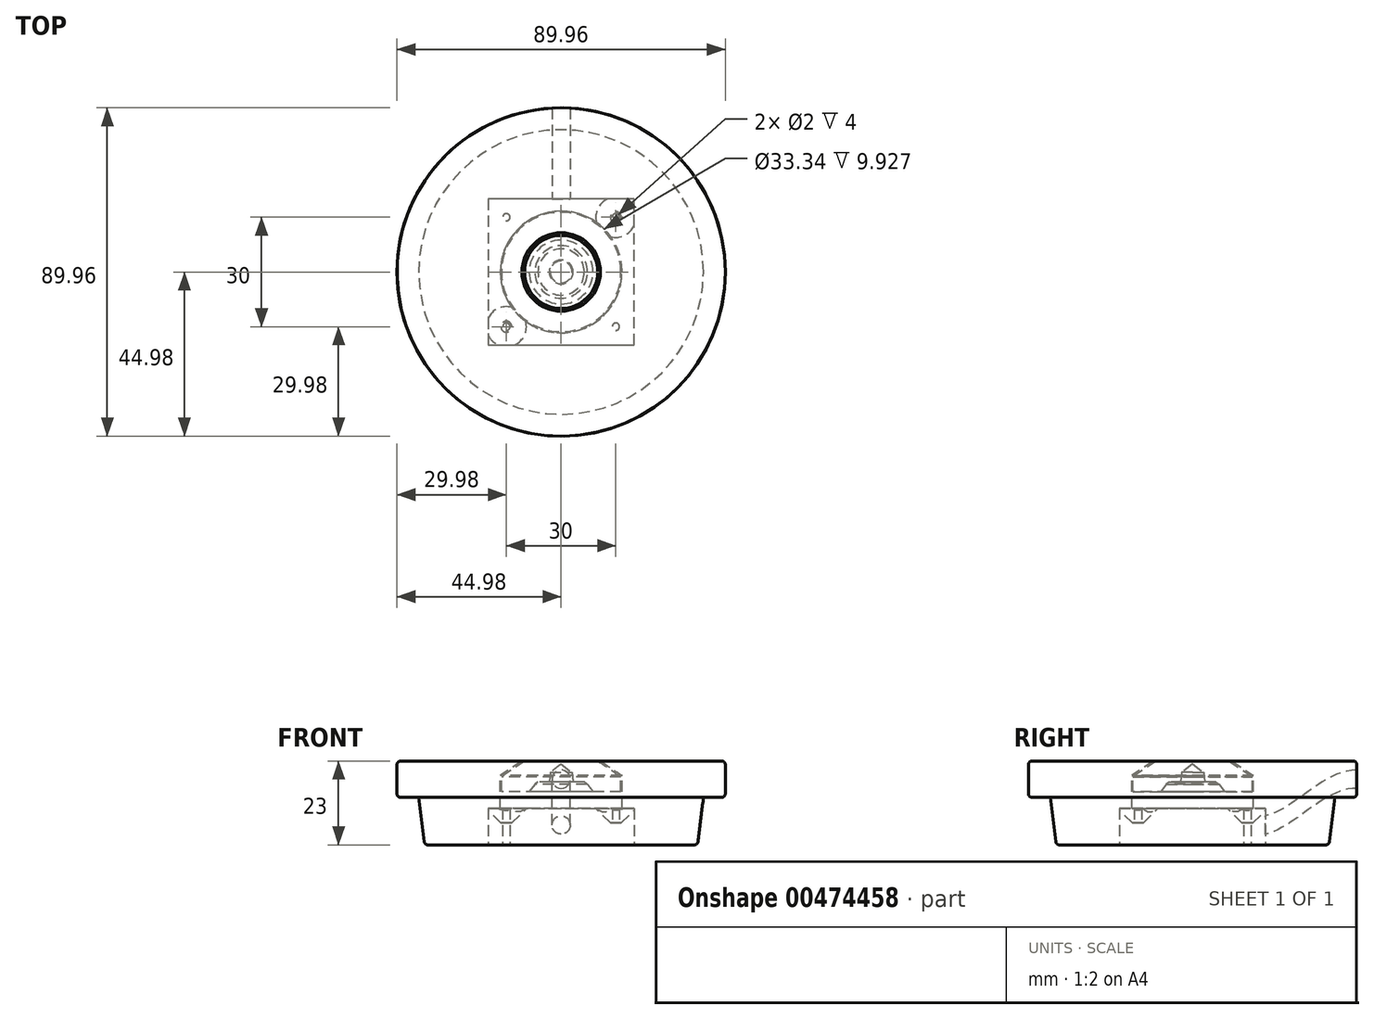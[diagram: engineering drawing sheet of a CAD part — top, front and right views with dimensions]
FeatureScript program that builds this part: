
annotation { "Feature Type Name" : "Feature", "Feature Type Description" : "" }
export const myFeature = defineFeature(function(context is Context, id is Id, definition is map)
    precondition{}
    {
        {
            var Q0;
            Q0=qCreatedBy(makeId("Right.planeOp"),FACE);
            var sketch = newSketch(context, id + "F0", { "sketchPlane" : qUnion([Q0])});
            skLineSegment(sketch, "E0", {"start": v(0, 0) * mm, "end": v(10, 0) * mm});
            skLineSegment(sketch, "E1", {"start": v(16.67, -4.03) * mm, "end": v(16.67, -10) * mm});
            skLineSegment(sketch, "E2", {"start": v(16.67, -10) * mm, "end": v(10, -10) * mm});
            skLineSegment(sketch, "E3", {"start": v(5, -3.55) * mm, "end": v(0, -3.55) * mm, "construction": true});
            skLineSegment(sketch, "E4", {"start": v(0, -3.55) * mm, "end": v(0, 0) * mm});
            skLineSegment(sketch, "E5.0", {"start": v(16.37, -4.33) * mm, "end": v(16.37, -10) * mm, "construction": true});
            skLineSegment(sketch, "E6", {"start": v(10.74, 0) * mm, "end": v(43.98, 0) * mm});
            skLineSegment(sketch, "E7", {"start": v(44.98, -1) * mm, "end": v(44.98, -9) * mm});
            skLineSegment(sketch, "E8", {"start": v(43.98, -10) * mm, "end": v(39, -10) * mm});
            skPoint(sketch, "E9.visualSharp", {"position": v(10, -3.55) * mm});
            skLineSegment(sketch, "E10", {"start": v(10, 0) * mm, "end": v(16.37, -4.33) * mm});
            skLineSegment(sketch, "E11.0", {"start": v(10.74, 0) * mm, "end": v(16.67, -4.03) * mm});
            skLineSegment(sketch, "E12", {"start": v(7.2, -6.38) * mm, "end": v(10, -10) * mm});
            skLineSegment(sketch, "E13", {"start": v(39, -10) * mm, "end": v(37.5, -22.12) * mm});
            skLineSegment(sketch, "E14", {"start": v(36.5, -23) * mm, "end": v(17.67, -23) * mm});
            skLineSegment(sketch, "E15", {"start": v(16.67, -22) * mm, "end": v(16.67, -10) * mm});
            skPoint(sketch, "E16.visualSharp", {"position": v(44.98, 0) * mm});
            skArc(sketch, "E16.filletArc", {"start": v(44.98, -1) * mm, "mid": v(44.69, -0.3) * mm, "end": v(43.98, 0) * mm});
            skPoint(sketch, "E17.visualSharp", {"position": v(44.98, -10) * mm});
            skArc(sketch, "E17.filletArc", {"start": v(43.98, -10) * mm, "mid": v(44.69, -9.7) * mm, "end": v(44.98, -9) * mm});
            skPoint(sketch, "E18.visualSharp", {"position": v(40.48, -10) * mm});
            skPoint(sketch, "E19.visualSharp", {"position": v(40.5, -23) * mm});
            skArc(sketch, "E19.filletArc", {"start": v(36.5, -23) * mm, "mid": v(37.17, -22.75) * mm, "end": v(37.5, -22.12) * mm});
            skPoint(sketch, "E20.visualSharp", {"position": v(16.67, -23) * mm});
            skArc(sketch, "E20.filletArc", {"start": v(16.67, -22) * mm, "mid": v(16.96, -22.7) * mm, "end": v(17.67, -23) * mm});
            skLineSegment(sketch, "E21", {"start": v(0, 0) * mm, "end": v(0, -40.81) * mm, "construction": true});
            skLineSegment(sketch, "E22", {"start": v(37.5, -22.12) * mm, "end": v(37.5, -26.5) * mm, "construction": true});
            skFitSpline(sketch, "E23", {"points": [v(44.98, -5) * mm, v(16.67, -18) * mm], "startDerivative": vector(-31.15, 0) * mm, "endDerivative": vector(-31.15, 0) * mm});
            skLineSegment(sketch, "E24", {"start": v(16.67, -10) * mm, "end": v(0, -10) * mm, "construction": true});
            skLineSegment(sketch, "E25", {"start": v(0, -10) * mm, "end": v(6, -10) * mm});
            skLineSegment(sketch, "E26", {"start": v(6, -10) * mm, "end": v(6, -6.7) * mm, "construction": true});
            skLineSegment(sketch, "E27", {"start": v(6, -6.7) * mm, "end": v(0, -6.7) * mm, "construction": true});
            skLineSegment(sketch, "E28", {"start": v(3, -6.7) * mm, "end": v(3, -3.55) * mm, "construction": true});
            skLineSegment(sketch, "E29", {"start": v(3, -3.55) * mm, "end": v(0, -3.55) * mm, "construction": true});
            skLineSegment(sketch, "E30", {"start": v(3, -6.7) * mm, "end": v(3, -3.15) * mm});
            skLineSegment(sketch, "E31", {"start": v(3, -3.15) * mm, "end": v(0, -3.15) * mm, "construction": true});
            skLineSegment(sketch, "E32", {"start": v(0, -11.2) * mm, "end": v(11, -11.2) * mm, "construction": true});
            skLineSegment(sketch, "E33", {"start": v(16.37, -8.4) * mm, "end": v(8.77, -8.4) * mm});
            skLineSegment(sketch, "E34", {"start": v(7.2, -6.38) * mm, "end": v(6.36, -5.74) * mm});
            skLineSegment(sketch, "E35", {"start": v(3, -3.15) * mm, "end": v(0, -0.84) * mm});
            skLineSegment(sketch, "E36", {"start": v(16.37, -4.33) * mm, "end": v(16.37, -8.4) * mm});
            skLineSegment(sketch, "E37", {"start": v(6.36, -5.74) * mm, "end": v(3.27, -5.74) * mm});
            skLineSegment(sketch, "E38", {"start": v(3.27, -5.74) * mm, "end": v(3, -3.15) * mm});
            skLineSegment(sketch, "E39.trimOffspring", {"start": v(3.52, -3.55) * mm, "end": v(3, -3.15) * mm});
            skSolve(sketch);
        }
        {
            var Q0;
            Q0=makeQuery(id+"F0.imprint","IMPRINT",FACE,{"disambiguationData":[TD([[makeQuery(id+"F0.imprint","IMPRINT",EDGE,{"derivedFrom":sQuery(id+"F0.wireOp",EDGE,"E0")}),-1.0]])]});
            var Q1;
            Q1=makeQuery(id+"F0.imprint","IMPRINT",FACE,{"disambiguationData":[TD([[makeQuery(id+"F0.imprint","IMPRINT",EDGE,{"derivedFrom":sQuery(id+"F0.wireOp",EDGE,"E1")}),1.0]])]});
            var Q2;
            Q2=makeQuery(id+"F0.imprint","IMPRINT",FACE,{"disambiguationData":[TD([[makeQuery(id+"F0.imprint","IMPRINT",EDGE,{"derivedFrom":sQuery(id+"F0.wireOp",EDGE,"E8")}),-1.0]])]});
            var Q3;
            Q3=sQuery(id+"F0.wireOp",EDGE,"E21");
            revolve(context, id + "F1", {"surfaceOperationType" : NewSurfaceOperationType.NEW, "entities" : qUnion([Q0, Q1, Q2]), "axis" : qUnion([Q3]), "revolveType" : RevolveType.FULL});
        }
        {
            var Q0;
            Q0=makeQuery(id+"F1.opRevolve","SWEPT_FACE",FACE,{"disambiguationData":[OSD([sQuery(id+"F0.wireOp",EDGE,"E14")])]});
            var sketch = newSketch(context, id + "F2", { "sketchPlane" : qUnion([Q0])});
            skLineSegment(sketch, "E40.left", {"start": v(0, 0) * mm, "end": v(0, -20) * mm, "construction": true});
            skLineSegment(sketch, "E41.MirrorCS", {"start": v(-20, 0) * mm, "end": v(-20, -20) * mm});
            skLineSegment(sketch, "E42.MirrorCS", {"start": v(0, -20) * mm, "end": v(-20, -20) * mm});
            skLineSegment(sketch, "E43", {"start": v(0, 0) * mm, "end": v(-20, 0) * mm, "construction": true});
            skLineSegment(sketch, "E44.MirrorCS", {"start": v(-20, 0) * mm, "end": v(-20, 20) * mm});
            skLineSegment(sketch, "E45.MirrorCS", {"start": v(0, 20) * mm, "end": v(-20, 20) * mm});
            skLineSegment(sketch, "E46.MirrorCS", {"start": v(20, 0) * mm, "end": v(20, -20) * mm});
            skLineSegment(sketch, "E47.MirrorCS", {"start": v(20, 0) * mm, "end": v(20, 20) * mm});
            skLineSegment(sketch, "E48.MirrorCS", {"start": v(0, 20) * mm, "end": v(20, 20) * mm});
            skLineSegment(sketch, "E49.MirrorCS", {"start": v(0, -20) * mm, "end": v(20, -20) * mm});
            skLineSegment(sketch, "E50", {"start": v(-20, 20) * mm, "end": v(-15, 15) * mm, "construction": true});
            skPoint(sketch, "E51.orphan", {"position": v(-10, 10) * mm});
            skCircle(sketch, "E52", {"center": v(-15, 15) * mm, "radius": 1 * mm});
            skCircle(sketch, "E53", {"center": v(-15, 15) * mm, "radius": 1.5 * mm});
            skCircle(sketch, "E54.MirrorC", {"center": v(-15, -15) * mm, "radius": 1.5 * mm});
            skCircle(sketch, "E55.MirrorC", {"center": v(-15, -15) * mm, "radius": 1 * mm});
            skCircle(sketch, "E56.MirrorC", {"center": v(15, 15) * mm, "radius": 1 * mm});
            skCircle(sketch, "E57.MirrorC", {"center": v(15, 15) * mm, "radius": 1.5 * mm});
            skCircle(sketch, "E58.MirrorC", {"center": v(15, -15) * mm, "radius": 1.5 * mm});
            skCircle(sketch, "E59.MirrorC", {"center": v(15, -15) * mm, "radius": 1 * mm});
            skSolve(sketch);
        }
        {
            var Q0;
            Q0=makeQuery(id+"F2.imprint","IMPRINT",FACE,{"disambiguationData":[TD([[makeQuery(id+"F2.imprint","IMPRINT",EDGE,{"derivedFrom":sQuery(id+"F2.wireOp",EDGE,"E41.MirrorCS")}),1.0]])]});
            var Q1;
            Q1=makeQuery(id+"F2.imprint","IMPRINT",FACE,{"disambiguationData":[TD([[makeQuery(id+"F2.imprint","IMPRINT",EDGE,{"derivedFrom":makeQuery(id+"F1.opRevolve","SWEPT_EDGE",EDGE,{"disambiguationData":[OSD([sQuery(id+"F0.wireOp",EDGE,"E14"),sQuery(id+"F0.wireOp",EDGE,"E20.filletArc")])]})}),-1.0]])]});
            var Q2;
            Q2=makeQuery(id+"F2.imprint","IMPRINT",FACE,{"disambiguationData":[TD([[makeQuery(id+"F2.imprint","IMPRINT",EDGE,{"derivedFrom":sQuery(id+"F2.wireOp",EDGE,"E52")}),1.0]])]});
            var Q3;
            Q3=makeQuery(id+"F2.imprint","IMPRINT",FACE,{"disambiguationData":[TD([[makeQuery(id+"F2.imprint","IMPRINT",EDGE,{"derivedFrom":sQuery(id+"F2.wireOp",EDGE,"E56.MirrorC")}),-1.0]])]});
            var Q4;
            Q4=makeQuery(id+"F2.imprint","IMPRINT",FACE,{"disambiguationData":[TD([[makeQuery(id+"F2.imprint","IMPRINT",EDGE,{"derivedFrom":sQuery(id+"F2.wireOp",EDGE,"E59.MirrorC")}),1.0]])]});
            var Q5;
            Q5=makeQuery(id+"F2.imprint","IMPRINT",FACE,{"disambiguationData":[TD([[makeQuery(id+"F2.imprint","IMPRINT",EDGE,{"derivedFrom":sQuery(id+"F2.wireOp",EDGE,"E55.MirrorC")}),-1.0]])]});
            extrude(context, id + "F3", {"entities" : qUnion([Q0, Q1, Q2, Q3, Q4, Q5]), "operationType" : NewBodyOperationType.REMOVE, "oppositeDirection" : true, "depth" : 10 * mm, "offsetDistance" : 25 * mm});
        }
        {
            var Q0;
            Q0=makeQuery(id+"F2.imprint","IMPRINT",FACE,{"disambiguationData":[TD([[makeQuery(id+"F2.imprint","IMPRINT",EDGE,{"derivedFrom":sQuery(id+"F2.wireOp",EDGE,"E41.MirrorCS")}),1.0]])]});
            var Q1;
            Q1=makeQuery(id+"F2.imprint","IMPRINT",FACE,{"disambiguationData":[TD([[makeQuery(id+"F2.imprint","IMPRINT",EDGE,{"derivedFrom":sQuery(id+"F2.wireOp",EDGE,"E52")}),-1.0]])]});
            var Q2;
            Q2=makeQuery(id+"F2.imprint","IMPRINT",FACE,{"disambiguationData":[TD([[makeQuery(id+"F2.imprint","IMPRINT",EDGE,{"derivedFrom":sQuery(id+"F2.wireOp",EDGE,"E52")}),1.0]])]});
            var Q3;
            Q3=makeQuery(id+"F2.imprint","IMPRINT",FACE,{"disambiguationData":[TD([[makeQuery(id+"F2.imprint","IMPRINT",EDGE,{"derivedFrom":sQuery(id+"F2.wireOp",EDGE,"E56.MirrorC")}),1.0]])]});
            var Q4;
            Q4=makeQuery(id+"F2.imprint","IMPRINT",FACE,{"disambiguationData":[TD([[makeQuery(id+"F2.imprint","IMPRINT",EDGE,{"derivedFrom":sQuery(id+"F2.wireOp",EDGE,"E56.MirrorC")}),-1.0]])]});
            var Q5;
            Q5=makeQuery(id+"F2.imprint","IMPRINT",FACE,{"disambiguationData":[TD([[makeQuery(id+"F2.imprint","IMPRINT",EDGE,{"derivedFrom":sQuery(id+"F2.wireOp",EDGE,"E58.MirrorC")}),1.0]])]});
            var Q6;
            Q6=makeQuery(id+"F2.imprint","IMPRINT",FACE,{"disambiguationData":[TD([[makeQuery(id+"F2.imprint","IMPRINT",EDGE,{"derivedFrom":sQuery(id+"F2.wireOp",EDGE,"E59.MirrorC")}),1.0]])]});
            var Q7;
            Q7=makeQuery(id+"F2.imprint","IMPRINT",FACE,{"disambiguationData":[TD([[makeQuery(id+"F2.imprint","IMPRINT",EDGE,{"derivedFrom":sQuery(id+"F2.wireOp",EDGE,"E54.MirrorC")}),-1.0]])]});
            var Q8;
            Q8=makeQuery(id+"F2.imprint","IMPRINT",FACE,{"disambiguationData":[TD([[makeQuery(id+"F2.imprint","IMPRINT",EDGE,{"derivedFrom":sQuery(id+"F2.wireOp",EDGE,"E55.MirrorC")}),-1.0]])]});
            extrude(context, id + "F4", {"entities" : qUnion([Q0, Q1, Q2, Q3, Q4, Q5, Q6, Q7, Q8]), "operationType" : NewBodyOperationType.REMOVE, "oppositeDirection" : true, "depth" : 6 * mm, "offsetDistance" : 25 * mm});
        }
        {
            var Q0;
            Q0=makeQuery(id+"F3.boolean.opBoolean","COPY",EDGE,{"derivedFrom":makeQuery(id+"F3.opExtrude","CAP_EDGE",EDGE,{"disambiguationData":[OSD([sQuery(id+"F2.wireOp",EDGE,"E54.MirrorC")])],"isStart":false})});
            var Q1;
            Q1=makeQuery(id+"F3.boolean.opBoolean","COPY",EDGE,{"derivedFrom":makeQuery(id+"F3.opExtrude","CAP_EDGE",EDGE,{"disambiguationData":[OSD([sQuery(id+"F2.wireOp",EDGE,"E58.MirrorC")])],"isStart":false})});
            var Q2;
            Q2=makeQuery(id+"F3.boolean.opBoolean","COPY",EDGE,{"derivedFrom":makeQuery(id+"F3.opExtrude","CAP_EDGE",EDGE,{"disambiguationData":[OSD([sQuery(id+"F2.wireOp",EDGE,"E57.MirrorC")])],"isStart":false})});
            var Q3;
            Q3=makeQuery(id+"F3.boolean.opBoolean","COPY",EDGE,{"derivedFrom":makeQuery(id+"F3.opExtrude","CAP_EDGE",EDGE,{"disambiguationData":[OSD([sQuery(id+"F2.wireOp",EDGE,"E53")])],"isStart":false})});
            chamfer(context, id + "F5", {"entities" : qUnion([Q0, Q1, Q2, Q3]), "width" : 4 * mm, "tangentPropagation" : true});
        }
        {
            var Q0;
            Q0=qCreatedBy(makeId("Front.planeOp"),FACE);
            var Q1;
            Q1=sQuery(id+"F0.wireOp",VERTEX,"E23.start");
            cPlane(context, id + "F6", {"entities" : qUnion([Q0, Q1]), "cplaneType" : CPlaneType.PLANE_POINT, "offset" : 25 * mm, "width" : 150 * mm, "height" : 150 * mm});
        }
        {
            var Q0;
            Q0=qCreatedBy(id+"F6.planeOp",FACE);
            var sketch = newSketch(context, id + "F7", { "sketchPlane" : qUnion([Q0])});
            skCircle(sketch, "E60", {"center": v(0, -5) * mm, "radius": 2.5 * mm});
            skSolve(sketch);
        }
        {
            var Q0;
            Q0=makeQuery(id+"F7.imprint","IMPRINT",FACE,{"disambiguationData":[TD([[makeQuery(id+"F7.imprint","IMPRINT",EDGE,{"derivedFrom":sQuery(id+"F7.wireOp",EDGE,"E60")}),1.0]])]});
            var Q1;
            Q1=sQuery(id+"F7.wireOp",EDGE,"E60");
            var Q2;
            Q2=sQuery(id+"F0.wireOp",EDGE,"E23");
            sweep(context, id + "F8", {"operationType" : NewBodyOperationType.REMOVE, "profiles" : qUnion([Q0]), "surfaceProfiles" : qUnion([Q1]), "path" : qUnion([Q2]), "keepProfileOrientation" : true});
        }
    });
